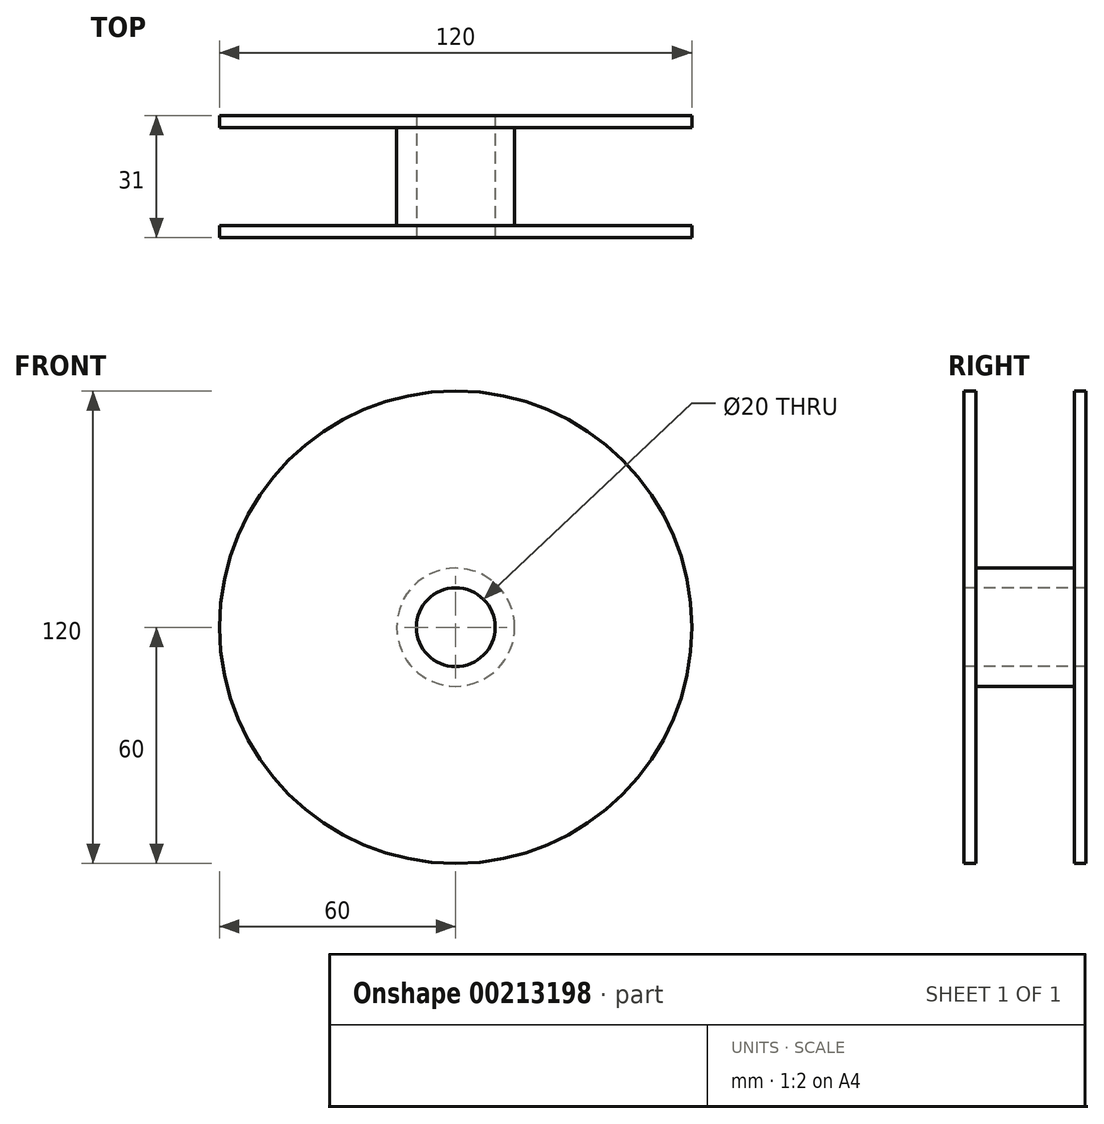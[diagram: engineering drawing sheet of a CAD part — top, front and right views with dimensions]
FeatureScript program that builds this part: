
annotation { "Feature Type Name" : "Feature", "Feature Type Description" : "" }
export const myFeature = defineFeature(function(context is Context, id is Id, definition is map)
    precondition{}
    {
        {
            var Q0;
            Q0=qCreatedBy(makeId("Right.planeOp"),FACE);
            var sketch = newSketch(context, id + "F0", { "sketchPlane" : qUnion([Q0])});
            skLineSegment(sketch, "E0", {"start": v(0, 60) * mm, "end": v(3, 60) * mm});
            skLineSegment(sketch, "E1", {"start": v(3, 60) * mm, "end": v(3, 15) * mm});
            skLineSegment(sketch, "E2", {"start": v(3, 15) * mm, "end": v(28, 15) * mm});
            skLineSegment(sketch, "E3", {"start": v(28, 15) * mm, "end": v(28, 60) * mm});
            skLineSegment(sketch, "E4", {"start": v(28, 60) * mm, "end": v(31, 60) * mm});
            skLineSegment(sketch, "E5", {"start": v(31, 60) * mm, "end": v(31, 10) * mm});
            skLineSegment(sketch, "E6", {"start": v(31, 10) * mm, "end": v(0, 10) * mm});
            skLineSegment(sketch, "E7", {"start": v(0, 60) * mm, "end": v(0, 10) * mm});
            skLineSegment(sketch, "E8", {"start": v(0, 0) * mm, "end": v(34.58, 0) * mm, "construction": true});
            skSolve(sketch);
        }
        {
            var Q0;
            Q0=makeQuery(id+"F0.imprint","IMPRINT",FACE,{"disambiguationData":[TD([[makeQuery(id+"F0.imprint","IMPRINT",EDGE,{"derivedFrom":sQuery(id+"F0.wireOp",EDGE,"E0")}),-1.0]])]});
            var Q1;
            Q1=sQuery(id+"F0.wireOp",EDGE,"E8");
            revolve(context, id + "F1", {"entities" : qUnion([Q0]), "axis" : qUnion([Q1]), "revolveType" : RevolveType.FULL});
        }
    });
